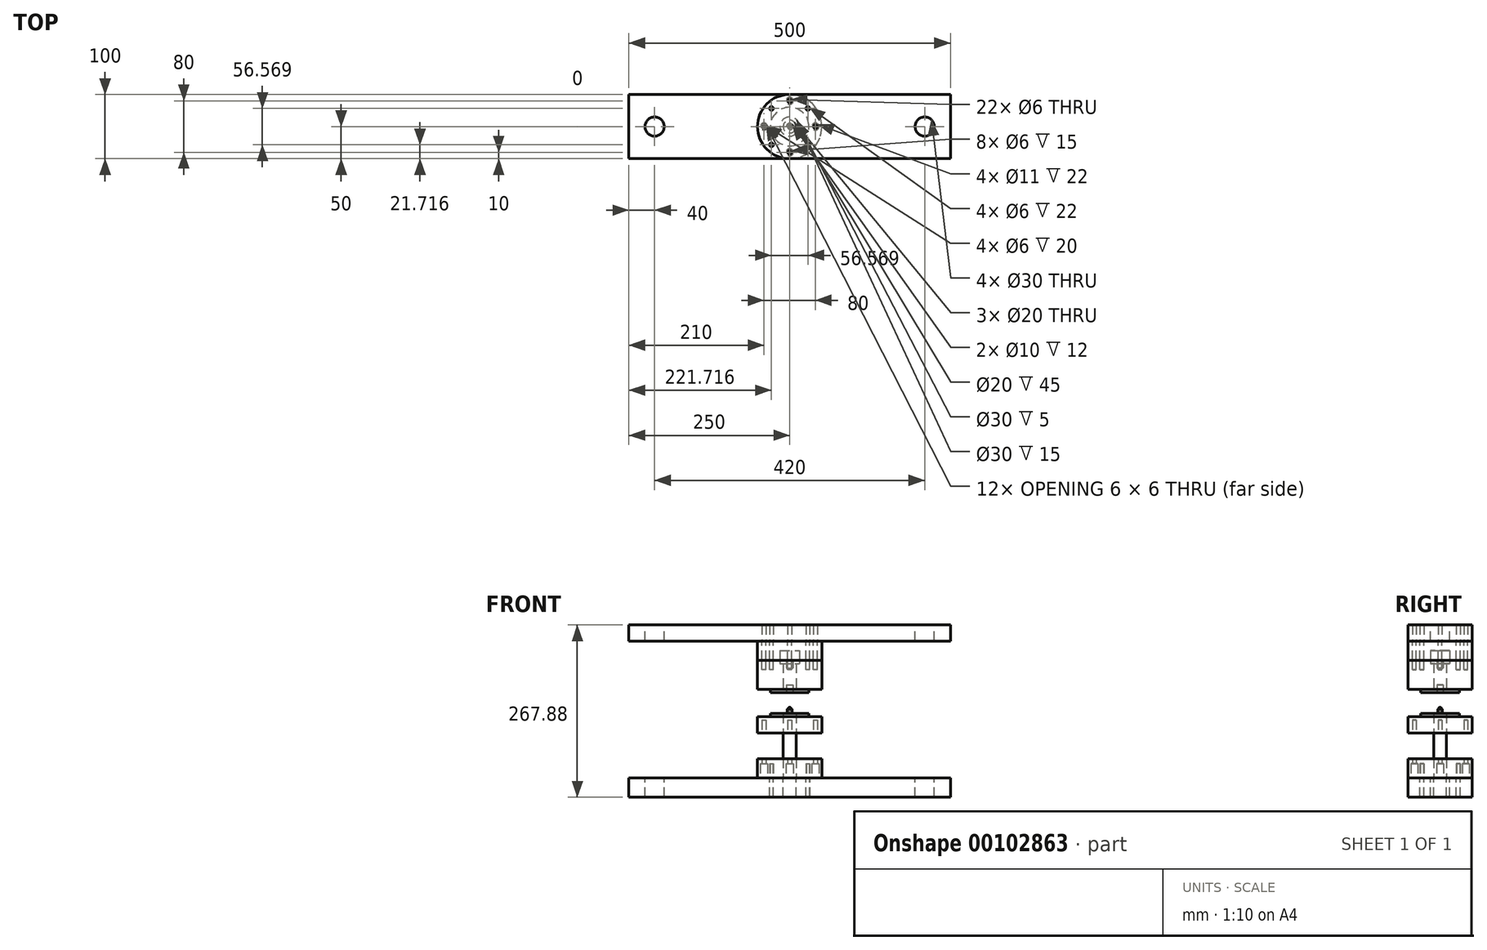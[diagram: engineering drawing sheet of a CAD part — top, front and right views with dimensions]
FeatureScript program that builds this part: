
annotation { "Feature Type Name" : "Feature", "Feature Type Description" : "" }
export const myFeature = defineFeature(function(context is Context, id is Id, definition is map)
    precondition{}
    {
        {
            var Q0;
            Q0=qCreatedBy(makeId("Front.planeOp"),FACE);
            var sketch = newSketch(context, id + "F0", { "sketchPlane" : qUnion([Q0])});
            skLineSegment(sketch, "E0", {"start": v(-30, 0) * mm, "end": v(-10, 0) * mm});
            skLineSegment(sketch, "E1", {"start": v(-30, 0) * mm, "end": v(-30, -5) * mm});
            skLineSegment(sketch, "E2", {"start": v(-50, -100) * mm, "end": v(0, -100) * mm});
            skLineSegment(sketch, "E3", {"start": v(0, -100) * mm, "end": v(0, 53.68) * mm, "construction": true});
            skPoint(sketch, "E3.endSnap0", {"position": v(0, -100) * mm});
            skLineSegment(sketch, "E4.0", {"start": v(-10, -100) * mm, "end": v(-10, 0) * mm});
            skLineSegment(sketch, "E5.0", {"start": v(-50, -30) * mm, "end": v(-10, -30) * mm});
            skLineSegment(sketch, "E6.0", {"start": v(-50, -70) * mm, "end": v(-10, -70) * mm});
            skLineSegment(sketch, "E7.0", {"start": v(-50, -100) * mm, "end": v(-50, -70) * mm});
            skLineSegment(sketch, "E8.0", {"start": v(-50, -5) * mm, "end": v(-30, -5) * mm});
            skLineSegment(sketch, "E9.0", {"start": v(-3.5, 0) * mm, "end": v(-3.5, 7) * mm});
            skLineSegment(sketch, "E10.0", {"start": v(-0.5, 10) * mm, "end": v(0, 10) * mm});
            skPoint(sketch, "E11.visualSharp", {"position": v(-3.5, 10) * mm});
            skArc(sketch, "E11.filletArc", {"start": v(-0.5, 10) * mm, "mid": v(-2.62, 9.12) * mm, "end": v(-3.5, 7) * mm});
            skPoint(sketch, "E12.visualSharp", {"position": v(3.5, 10) * mm});
            skLineSegment(sketch, "E13", {"start": v(-10, 0) * mm, "end": v(-3.5, 0) * mm});
            skLineSegment(sketch, "E14.trimOffspring", {"start": v(-50, -30) * mm, "end": v(-50, -5) * mm});
            skPoint(sketch, "E15.0.start.orphan", {"position": v(50, -100) * mm});
            skLineSegment(sketch, "E16", {"start": v(0, -100) * mm, "end": v(0, 10) * mm});
            skPoint(sketch, "E12.filletArc.end.orphan", {"position": v(0.5, 10) * mm});
            skSolve(sketch);
        }
        {
            var Q0;
            {var subQ2=sQuery(id+"F0.wireOp",EDGE,"E0");Q0=makeQuery(id+"F0.imprint","IMPRINT",FACE,{"disambiguationData":[TD([[makeQuery(id+"F0.imprint","IMPRINT",EDGE,{"derivedFrom":subQ2}),-1.0]])]});}
            var Q1;
            Q1=sQuery(id+"F0.wireOp",EDGE,"E3");
            revolve(context, id + "F1", {"entities" : qUnion([Q0]), "axis" : qUnion([Q1]), "revolveType" : RevolveType.FULL});
        }
        {
            var Q0;
            Q0=makeQuery(id+"F0.imprint","IMPRINT",FACE,{"disambiguationData":[TD([[makeQuery(id+"F0.imprint","IMPRINT",EDGE,{"derivedFrom":sQuery(id+"F0.wireOp",EDGE,"E9.0")}),-1.0]])]});
            var Q1;
            Q1=sQuery(id+"F0.wireOp",EDGE,"E3");
            revolve(context, id + "F2", {"entities" : qUnion([Q0]), "axis" : qUnion([Q1]), "revolveType" : RevolveType.FULL});
        }
        {
            var Q0;
            {var subQ4=sQuery(id+"F0.wireOp",EDGE,"E6.0");Q0=makeQuery(id+"F0.imprint","IMPRINT",FACE,{"disambiguationData":[TD([[makeQuery(id+"F0.imprint","IMPRINT",EDGE,{"derivedFrom":subQ4}),-1.0]])]});}
            var Q1;
            Q1=sQuery(id+"F0.wireOp",EDGE,"E3");
            revolve(context, id + "F3", {"entities" : qUnion([Q0]), "axis" : qUnion([Q1]), "revolveType" : RevolveType.FULL});
        }
        {
            var Q0;
            Q0=makeQuery(id+"F3.opRevolve","SWEPT_FACE",FACE,{"disambiguationData":[OSD([sQuery(id+"F0.wireOp",EDGE,"E2")])]});
            var sketch = newSketch(context, id + "F4", { "sketchPlane" : qUnion([Q0])});
            skCircle(sketch, "E17", {"center": v(-40, 0) * mm, "radius": 3 * mm});
            skCircle(sketch, "E18", {"center": v(0, 0) * mm, "radius": 40 * mm, "construction": true});
            skCircle(sketch, "E19.1.0", {"center": v(0, -40) * mm, "radius": 3 * mm});
            skCircle(sketch, "E19.2.0", {"center": v(40, 0) * mm, "radius": 3 * mm});
            skCircle(sketch, "E19.3.0", {"center": v(0, 40) * mm, "radius": 3 * mm});
            skCircle(sketch, "E20", {"center": v(-40, 0) * mm, "radius": 5.5 * mm});
            skCircle(sketch, "E21", {"center": v(0, -40) * mm, "radius": 5.5 * mm});
            skCircle(sketch, "E22", {"center": v(40, 0) * mm, "radius": 5.5 * mm});
            skCircle(sketch, "E23", {"center": v(0, 40) * mm, "radius": 5.5 * mm});
            skCircle(sketch, "E24.1.0", {"center": v(-28.28, 28.28) * mm, "radius": 3 * mm});
            skCircle(sketch, "E24.3.0", {"center": v(-28.28, -28.28) * mm, "radius": 3 * mm});
            skCircle(sketch, "E24.5.0", {"center": v(28.28, -28.28) * mm, "radius": 3 * mm});
            skCircle(sketch, "E24.7.0", {"center": v(28.28, 28.28) * mm, "radius": 3 * mm});
            skLineSegment(sketch, "E25.bottom", {"start": v(-250, -50) * mm, "end": v(250, -50) * mm});
            skLineSegment(sketch, "E25.top", {"start": v(-250, 50) * mm, "end": v(250, 50) * mm});
            skLineSegment(sketch, "E25.left", {"start": v(-250, -50) * mm, "end": v(-250, 50) * mm});
            skLineSegment(sketch, "E25.right", {"start": v(250, -50) * mm, "end": v(250, 50) * mm});
            skCircle(sketch, "E26", {"center": v(-28.28, 28.28) * mm, "radius": 3.15 * mm});
            skCircle(sketch, "E27", {"center": v(28.28, 28.28) * mm, "radius": 2.5 * mm});
            skCircle(sketch, "E28", {"center": v(-28.28, -28.28) * mm, "radius": 2.5 * mm});
            skCircle(sketch, "E29", {"center": v(28.28, -28.28) * mm, "radius": 3.15 * mm});
            skSolve(sketch);
        }
        {
            var Q0;
            Q0=makeQuery(id+"F4.imprint","IMPRINT",FACE,{"disambiguationData":[TD([[makeQuery(id+"F4.imprint","IMPRINT",EDGE,{"derivedFrom":sQuery(id+"F4.wireOp",EDGE,"E19.1.0")}),1.0]])]});
            var Q1;
            Q1=makeQuery(id+"F4.imprint","IMPRINT",FACE,{"disambiguationData":[TD([[makeQuery(id+"F4.imprint","IMPRINT",EDGE,{"derivedFrom":sQuery(id+"F4.wireOp",EDGE,"E17")}),1.0]])]});
            var Q2;
            Q2=makeQuery(id+"F4.imprint","IMPRINT",FACE,{"disambiguationData":[TD([[makeQuery(id+"F4.imprint","IMPRINT",EDGE,{"derivedFrom":sQuery(id+"F4.wireOp",EDGE,"E19.3.0")}),1.0]])]});
            var Q3;
            Q3=makeQuery(id+"F4.imprint","IMPRINT",FACE,{"disambiguationData":[TD([[makeQuery(id+"F4.imprint","IMPRINT",EDGE,{"derivedFrom":sQuery(id+"F4.wireOp",EDGE,"E19.2.0")}),1.0]])]});
            extrude(context, id + "F5", {"entities" : qUnion([Q0, Q1, Q2, Q3]), "operationType" : NewBodyOperationType.REMOVE, "oppositeDirection" : true, "depth" : 90 * mm});
        }
        {
            var Q0;
            Q0=makeQuery(id+"F4.imprint","IMPRINT",FACE,{"disambiguationData":[TD([[makeQuery(id+"F4.imprint","IMPRINT",EDGE,{"derivedFrom":sQuery(id+"F4.wireOp",EDGE,"E20")}),1.0]])]});
            var Q1;
            Q1=makeQuery(id+"F4.imprint","IMPRINT",FACE,{"disambiguationData":[TD([[makeQuery(id+"F4.imprint","IMPRINT",EDGE,{"derivedFrom":sQuery(id+"F4.wireOp",EDGE,"E21")}),1.0]])]});
            var Q2;
            Q2=makeQuery(id+"F4.imprint","IMPRINT",FACE,{"disambiguationData":[TD([[makeQuery(id+"F4.imprint","IMPRINT",EDGE,{"derivedFrom":sQuery(id+"F4.wireOp",EDGE,"E22")}),1.0]])]});
            var Q3;
            Q3=makeQuery(id+"F4.imprint","IMPRINT",FACE,{"disambiguationData":[TD([[makeQuery(id+"F4.imprint","IMPRINT",EDGE,{"derivedFrom":sQuery(id+"F4.wireOp",EDGE,"E19.3.0")}),-1.0]])]});
            var Q4;
            Q4=makeQuery(id+"F4.imprint","IMPRINT",FACE,{"disambiguationData":[TD([[makeQuery(id+"F4.imprint","IMPRINT",EDGE,{"derivedFrom":sQuery(id+"F4.wireOp",EDGE,"E24.5.0")}),1.0]])]});
            var Q5;
            Q5=makeQuery(id+"F4.imprint","IMPRINT",FACE,{"disambiguationData":[TD([[makeQuery(id+"F4.imprint","IMPRINT",EDGE,{"derivedFrom":sQuery(id+"F4.wireOp",EDGE,"E24.3.0")}),1.0]])]});
            var Q6;
            Q6=makeQuery(id+"F4.imprint","IMPRINT",FACE,{"disambiguationData":[TD([[makeQuery(id+"F4.imprint","IMPRINT",EDGE,{"derivedFrom":sQuery(id+"F4.wireOp",EDGE,"E24.1.0")}),1.0]])]});
            var Q7;
            Q7=makeQuery(id+"F4.imprint","IMPRINT",FACE,{"disambiguationData":[TD([[makeQuery(id+"F4.imprint","IMPRINT",EDGE,{"derivedFrom":sQuery(id+"F4.wireOp",EDGE,"E24.7.0")}),1.0]])]});
            extrude(context, id + "F6", {"entities" : qUnion([Q0, Q1, Q2, Q3, Q4, Q5, Q6, Q7]), "operationType" : NewBodyOperationType.REMOVE, "oppositeDirection" : true, "depth" : 22 * mm});
        }
        {
            var Q0;
            Q0=makeQuery(id+"F4.imprint","IMPRINT",FACE,{"disambiguationData":[TD([[makeQuery(id+"F4.imprint","IMPRINT",EDGE,{"derivedFrom":sQuery(id+"F4.wireOp",EDGE,"E25.bottom")}),1.0]])]});
            var Q1;
            Q1=makeQuery(id+"F4.imprint","IMPRINT",FACE,{"disambiguationData":[TD([[makeQuery(id+"F4.imprint","IMPRINT",EDGE,{"derivedFrom":sQuery(id+"F4.wireOp",EDGE,"E20")}),-1.0]])]});
            var Q2;
            Q2=makeQuery(id+"F4.imprint","IMPRINT",FACE,{"disambiguationData":[TD([[makeQuery(id+"F4.imprint","IMPRINT",EDGE,{"derivedFrom":sQuery(id+"F4.wireOp",EDGE,"E21")}),1.0]])]});
            var Q3;
            Q3=makeQuery(id+"F4.imprint","IMPRINT",FACE,{"disambiguationData":[TD([[makeQuery(id+"F4.imprint","IMPRINT",EDGE,{"derivedFrom":sQuery(id+"F4.wireOp",EDGE,"E19.1.0")}),1.0]])]});
            var Q4;
            Q4=makeQuery(id+"F4.imprint","IMPRINT",FACE,{"disambiguationData":[TD([[makeQuery(id+"F4.imprint","IMPRINT",EDGE,{"derivedFrom":sQuery(id+"F4.wireOp",EDGE,"E22")}),1.0]])]});
            var Q5;
            Q5=makeQuery(id+"F4.imprint","IMPRINT",FACE,{"disambiguationData":[TD([[makeQuery(id+"F4.imprint","IMPRINT",EDGE,{"derivedFrom":sQuery(id+"F4.wireOp",EDGE,"E19.2.0")}),1.0]])]});
            var Q6;
            Q6=makeQuery(id+"F4.imprint","IMPRINT",FACE,{"disambiguationData":[TD([[makeQuery(id+"F4.imprint","IMPRINT",EDGE,{"derivedFrom":sQuery(id+"F4.wireOp",EDGE,"E19.3.0")}),-1.0]])]});
            var Q7;
            Q7=makeQuery(id+"F4.imprint","IMPRINT",FACE,{"disambiguationData":[TD([[makeQuery(id+"F4.imprint","IMPRINT",EDGE,{"derivedFrom":sQuery(id+"F4.wireOp",EDGE,"E19.3.0")}),1.0]])]});
            var Q8;
            Q8=makeQuery(id+"F4.imprint","IMPRINT",FACE,{"disambiguationData":[TD([[makeQuery(id+"F4.imprint","IMPRINT",EDGE,{"derivedFrom":sQuery(id+"F4.wireOp",EDGE,"E20")}),1.0]])]});
            var Q9;
            Q9=makeQuery(id+"F4.imprint","IMPRINT",FACE,{"disambiguationData":[TD([[makeQuery(id+"F4.imprint","IMPRINT",EDGE,{"derivedFrom":sQuery(id+"F4.wireOp",EDGE,"E17")}),1.0]])]});
            extrude(context, id + "F7", {"entities" : qUnion([Q0, Q1, Q2, Q3, Q4, Q5, Q6, Q7, Q8, Q9]), "depth" : 30 * mm});
        }
        {
            var Q0;
            Q0=qCreatedBy(makeId("Front.planeOp"),FACE);
            var sketch = newSketch(context, id + "F8", { "sketchPlane" : qUnion([Q0])});
            skLineSegment(sketch, "E30.0", {"start": v(0, -100) * mm, "end": v(0, 70.88) * mm});
            skLineSegment(sketch, "E31", {"start": v(-5, 32.88) * mm, "end": v(-30, 32.88) * mm});
            skPoint(sketch, "E31.endSnap0", {"position": v(0, 32.88) * mm});
            skLineSegment(sketch, "E32.0", {"start": v(-50, 37.88) * mm, "end": v(-50, 82.88) * mm});
            skLineSegment(sketch, "E33.0", {"start": v(-30, 32.88) * mm, "end": v(-30, 37.88) * mm});
            skLineSegment(sketch, "E34.0", {"start": v(-5, 82.88) * mm, "end": v(-50, 82.88) * mm});
            skLineSegment(sketch, "E35.trimOffspring", {"start": v(-30, 37.88) * mm, "end": v(-50, 37.88) * mm});
            skLineSegment(sketch, "E36.0", {"start": v(-10, 32.88) * mm, "end": v(-10, 77.88) * mm});
            skLineSegment(sketch, "E37.0", {"start": v(-10, 77.88) * mm, "end": v(-15, 77.88) * mm});
            skLineSegment(sketch, "E38.0", {"start": v(-15, 77.88) * mm, "end": v(-15, 82.88) * mm});
            skLineSegment(sketch, "E39.0", {"start": v(0, 112.88) * mm, "end": v(-50, 112.88) * mm});
            skLineSegment(sketch, "E40", {"start": v(-15, 82.88) * mm, "end": v(-15, 97.88) * mm});
            skLineSegment(sketch, "E41", {"start": v(-50, 82.88) * mm, "end": v(-50, 112.88) * mm});
            skLineSegment(sketch, "E42.0", {"start": v(0, 97.88) * mm, "end": v(-15, 97.88) * mm});
            skLineSegment(sketch, "E43.0", {"start": v(-5, 32.88) * mm, "end": v(-5, 44.88) * mm});
            skLineSegment(sketch, "E44.0", {"start": v(0, 44.88) * mm, "end": v(-5, 44.88) * mm});
            skLineSegment(sketch, "E45.0", {"start": v(-5, -100) * mm, "end": v(-5, 82.88) * mm});
            skLineSegment(sketch, "E46.0", {"start": v(0, 70.88) * mm, "end": v(-5, 70.88) * mm});
            skLineSegment(sketch, "E47.trimOffspring", {"start": v(0, 97.88) * mm, "end": v(0, 112.88) * mm});
            skSolve(sketch);
        }
        {
            var Q0;
            {var subQ3=sQuery(id+"F8.wireOp",EDGE,"E36.0");Q0=makeQuery(id+"F8.imprint","IMPRINT",FACE,{"disambiguationData":[TD([[makeQuery(id+"F8.imprint","IMPRINT",EDGE,{"derivedFrom":subQ3}),-1.0]])]});}
            var Q1;
            {var subQ2=sQuery(id+"F8.wireOp",EDGE,"E44.0");Q1=makeQuery(id+"F8.imprint","IMPRINT",FACE,{"disambiguationData":[TD([[makeQuery(id+"F8.imprint","IMPRINT",EDGE,{"derivedFrom":subQ2}),-1.0]])]});}
            var Q2;
            Q2=sQuery(id+"F8.wireOp",EDGE,"E30.0");
            revolve(context, id + "F9", {"entities" : qUnion([Q0, Q1]), "axis" : qUnion([Q2]), "revolveType" : RevolveType.FULL});
        }
        {
            var Q0;
            {var subQ1=sQuery(id+"F8.wireOp",EDGE,"E32.0");Q0=makeQuery(id+"F8.imprint","IMPRINT",FACE,{"disambiguationData":[TD([[makeQuery(id+"F8.imprint","IMPRINT",EDGE,{"derivedFrom":subQ1}),-1.0]])]});}
            var Q1;
            Q1=sQuery(id+"F8.wireOp",EDGE,"E30.0");
            revolve(context, id + "F10", {"entities" : qUnion([Q0]), "axis" : qUnion([Q1]), "revolveType" : RevolveType.FULL});
        }
        {
            var Q0;
            Q0=makeQuery(id+"F8.imprint","IMPRINT",FACE,{"disambiguationData":[TD([[makeQuery(id+"F8.imprint","IMPRINT",EDGE,{"derivedFrom":sQuery(id+"F8.wireOp",EDGE,"E39.0")}),1.0]])]});
            var Q1;
            Q1=sQuery(id+"F8.wireOp",EDGE,"E47.trimOffspring");
            revolve(context, id + "F11", {"entities" : qUnion([Q0]), "axis" : qUnion([Q1]), "revolveType" : RevolveType.FULL});
        }
        {
            var Q0;
            Q0=makeQuery(id+"F11.opRevolve","SWEPT_FACE",FACE,{"disambiguationData":[OSD([sQuery(id+"F8.wireOp",EDGE,"E39.0")])]});
            var sketch = newSketch(context, id + "F12", { "sketchPlane" : qUnion([Q0])});
            skCircle(sketch, "E48", {"center": v(0, 0) * mm, "radius": 40 * mm, "construction": true});
            skCircle(sketch, "E49", {"center": v(-40, 0) * mm, "radius": 3 * mm});
            skCircle(sketch, "E50.1.0", {"center": v(-28.28, -28.28) * mm, "radius": 3 * mm});
            skCircle(sketch, "E50.2.0", {"center": v(0, -40) * mm, "radius": 3 * mm});
            skCircle(sketch, "E50.3.0", {"center": v(28.28, -28.28) * mm, "radius": 3 * mm});
            skCircle(sketch, "E50.4.0", {"center": v(40, 0) * mm, "radius": 3 * mm});
            skCircle(sketch, "E50.5.0", {"center": v(28.28, 28.28) * mm, "radius": 3 * mm});
            skCircle(sketch, "E50.6.0", {"center": v(0, 40) * mm, "radius": 3 * mm});
            skCircle(sketch, "E50.7.0", {"center": v(-28.28, 28.28) * mm, "radius": 3 * mm});
            skLineSegment(sketch, "E51.bottom", {"start": v(250, 50) * mm, "end": v(-250, 50) * mm});
            skLineSegment(sketch, "E51.top", {"start": v(250, -50) * mm, "end": v(-250, -50) * mm});
            skLineSegment(sketch, "E51.left", {"start": v(250, 50) * mm, "end": v(250, -50) * mm});
            skLineSegment(sketch, "E51.right", {"start": v(-250, 50) * mm, "end": v(-250, -50) * mm});
            skSolve(sketch);
        }
        {
            var Q0;
            Q0=makeQuery(id+"F12.imprint","IMPRINT",FACE,{"disambiguationData":[TD([[makeQuery(id+"F12.imprint","IMPRINT",EDGE,{"derivedFrom":sQuery(id+"F12.wireOp",EDGE,"E50.1.0")}),1.0]])]});
            var Q1;
            Q1=makeQuery(id+"F12.imprint","IMPRINT",FACE,{"disambiguationData":[TD([[makeQuery(id+"F12.imprint","IMPRINT",EDGE,{"derivedFrom":sQuery(id+"F12.wireOp",EDGE,"E50.3.0")}),1.0]])]});
            var Q2;
            Q2=makeQuery(id+"F12.imprint","IMPRINT",FACE,{"disambiguationData":[TD([[makeQuery(id+"F12.imprint","IMPRINT",EDGE,{"derivedFrom":sQuery(id+"F12.wireOp",EDGE,"E50.5.0")}),1.0]])]});
            var Q3;
            Q3=makeQuery(id+"F12.imprint","IMPRINT",FACE,{"disambiguationData":[TD([[makeQuery(id+"F12.imprint","IMPRINT",EDGE,{"derivedFrom":sQuery(id+"F12.wireOp",EDGE,"E50.7.0")}),1.0]])]});
            var Q4;
            Q4=makeQuery(id+"F12.imprint","IMPRINT",FACE,{"disambiguationData":[TD([[makeQuery(id+"F12.imprint","IMPRINT",EDGE,{"derivedFrom":sQuery(id+"F12.wireOp",EDGE,"E49")}),1.0]])]});
            var Q5;
            Q5=makeQuery(id+"F12.imprint","IMPRINT",FACE,{"disambiguationData":[TD([[makeQuery(id+"F12.imprint","IMPRINT",EDGE,{"derivedFrom":sQuery(id+"F12.wireOp",EDGE,"E50.2.0")}),1.0]])]});
            var Q6;
            Q6=makeQuery(id+"F12.imprint","IMPRINT",FACE,{"disambiguationData":[TD([[makeQuery(id+"F12.imprint","IMPRINT",EDGE,{"derivedFrom":sQuery(id+"F12.wireOp",EDGE,"E50.4.0")}),1.0]])]});
            var Q7;
            Q7=makeQuery(id+"F12.imprint","IMPRINT",FACE,{"disambiguationData":[TD([[makeQuery(id+"F12.imprint","IMPRINT",EDGE,{"derivedFrom":sQuery(id+"F12.wireOp",EDGE,"E50.6.0")}),1.0]])]});
            extrude(context, id + "F13", {"entities" : qUnion([Q0, Q1, Q2, Q3, Q4, Q5, Q6, Q7]), "operationType" : NewBodyOperationType.REMOVE, "oppositeDirection" : true, "depth" : 45 * mm});
        }
        {
            var Q0;
            {var subQ0=sQuery(id+"F12.wireOp",EDGE,"E51.right");Q0=makeQuery(id+"F12.imprint","IMPRINT",FACE,{"disambiguationData":[TD([[makeQuery(id+"F12.imprint","IMPRINT",EDGE,{"derivedFrom":subQ0}),1.0]])]});}
            var Q1;
            {var subQ0=sQuery(id+"F12.wireOp",EDGE,"E51.left");Q1=makeQuery(id+"F12.imprint","IMPRINT",FACE,{"disambiguationData":[TD([[makeQuery(id+"F12.imprint","IMPRINT",EDGE,{"derivedFrom":subQ0}),-1.0]])]});}
            var Q2;
            Q2=makeQuery(id+"F12.imprint","IMPRINT",FACE,{"disambiguationData":[TD([[makeQuery(id+"F12.imprint","IMPRINT",EDGE,{"derivedFrom":sQuery(id+"F12.wireOp",EDGE,"E49")}),-1.0]])]});
            extrude(context, id + "F14", {"entities" : qUnion([Q0, Q1, Q2]), "depth" : 25 * mm});
        }
        {
            var Q0;
            Q0=makeQuery(id+"F14.opExtrude","CAP_FACE",FACE,{"disambiguationData":[OSD([sQuery(id+"F12.wireOp",EDGE,"E49"),sQuery(id+"F12.wireOp",EDGE,"E50.1.0"),sQuery(id+"F12.wireOp",EDGE,"E50.2.0"),sQuery(id+"F12.wireOp",EDGE,"E50.3.0"),sQuery(id+"F12.wireOp",EDGE,"E50.4.0"),sQuery(id+"F12.wireOp",EDGE,"E50.5.0"),sQuery(id+"F12.wireOp",EDGE,"E50.6.0"),sQuery(id+"F12.wireOp",EDGE,"E50.7.0"),sQuery(id+"F12.wireOp",EDGE,"E51.bottom"),sQuery(id+"F12.wireOp",EDGE,"E51.top"),sQuery(id+"F12.wireOp",EDGE,"E51.left"),sQuery(id+"F12.wireOp",EDGE,"E51.right")])],"isStart":false});
            var sketch = newSketch(context, id + "F15", { "sketchPlane" : qUnion([Q0])});
            skCircle(sketch, "E52", {"center": v(-210, 0) * mm, "radius": 15 * mm});
            skCircle(sketch, "E53", {"center": v(210, 0) * mm, "radius": 15 * mm});
            skSolve(sketch);
        }
        {
            var Q0;
            Q0=makeQuery(id+"F15.imprint","IMPRINT",FACE,{"disambiguationData":[TD([[makeQuery(id+"F15.imprint","IMPRINT",EDGE,{"derivedFrom":sQuery(id+"F15.wireOp",EDGE,"E53")}),1.0]])]});
            var Q1;
            Q1=makeQuery(id+"F15.imprint","IMPRINT",FACE,{"disambiguationData":[TD([[makeQuery(id+"F15.imprint","IMPRINT",EDGE,{"derivedFrom":sQuery(id+"F15.wireOp",EDGE,"E52")}),1.0]])]});
            extrude(context, id + "F16", {"entities" : qUnion([Q0, Q1]), "operationType" : NewBodyOperationType.REMOVE, "oppositeDirection" : true, "depth" : 300 * mm});
        }
    });
